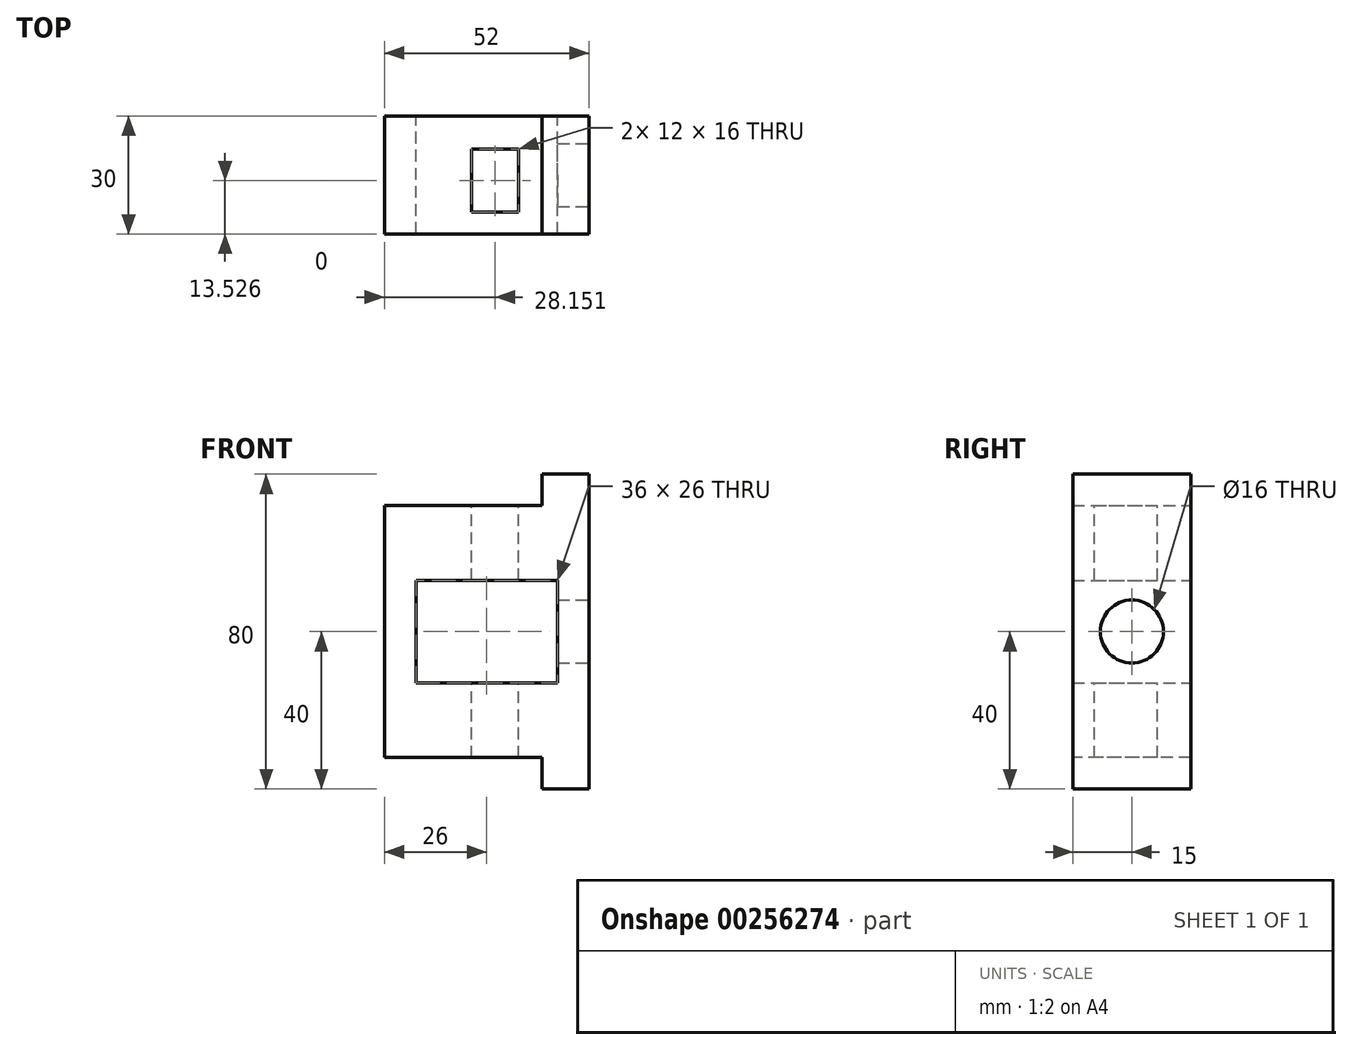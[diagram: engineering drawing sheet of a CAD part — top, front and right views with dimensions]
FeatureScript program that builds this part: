
annotation { "Feature Type Name" : "Feature", "Feature Type Description" : "" }
export const myFeature = defineFeature(function(context is Context, id is Id, definition is map)
    precondition{}
    {
        {
            var Q0;
            Q0=qCreatedBy(makeId("Right.planeOp"),FACE);
            var sketch = newSketch(context, id + "F0", { "sketchPlane" : qUnion([Q0])});
            skLineSegment(sketch, "E0.bottom", {"start": v(15, 32) * mm, "end": v(-15, 32) * mm});
            skLineSegment(sketch, "E0.top", {"start": v(15, -32) * mm, "end": v(-15, -32) * mm});
            skLineSegment(sketch, "E0.left", {"start": v(15, 32) * mm, "end": v(15, -32) * mm});
            skLineSegment(sketch, "E0.right", {"start": v(-15, 32) * mm, "end": v(-15, -32) * mm});
            skPoint(sketch, "E0.middle", {"position": v(0, 0) * mm});
            skSolve(sketch);
        }
        {
            var Q0;
            Q0=makeQuery(id+"F0.imprint","IMPRINT",FACE,{"disambiguationData":[TD([[makeQuery(id+"F0.imprint","IMPRINT",EDGE,{"derivedFrom":sQuery(id+"F0.wireOp",EDGE,"E0.bottom")}),1.0]])]});
            extrude(context, id + "F1", {"entities" : qUnion([Q0]), "depth" : 52 * mm});
        }
        {
            var Q0;
            Q0=makeQuery(id+"F1.opExtrude","SWEPT_FACE",FACE,{"disambiguationData":[OSD([sQuery(id+"F0.wireOp",EDGE,"E0.left")])]});
            var sketch = newSketch(context, id + "F2", { "sketchPlane" : qUnion([Q0])});
            skLineSegment(sketch, "E1.bottom", {"start": v(-8, -13) * mm, "end": v(-44, -13) * mm});
            skLineSegment(sketch, "E1.top", {"start": v(-8, 13) * mm, "end": v(-44, 13) * mm});
            skLineSegment(sketch, "E1.left", {"start": v(-8, -13) * mm, "end": v(-8, 13) * mm});
            skLineSegment(sketch, "E1.right", {"start": v(-44, -13) * mm, "end": v(-44, 13) * mm});
            skPoint(sketch, "E1.middle", {"position": v(-26, 0) * mm});
            skPoint(sketch, "E1.middle.positionSnap0", {"position": v(-26, 32) * mm});
            skPoint(sketch, "E1.middle.positionSnap1", {"position": v(-52, 0) * mm});
            skPoint(sketch, "E1.centerSnap0", {"position": v(-26, 32) * mm});
            skPoint(sketch, "E1.centerSnap1", {"position": v(-52, 0) * mm});
            skSolve(sketch);
        }
        {
            var Q0;
            Q0=makeQuery(id+"F2.imprint","IMPRINT",FACE,{"disambiguationData":[TD([[makeQuery(id+"F2.imprint","IMPRINT",EDGE,{"derivedFrom":sQuery(id+"F2.wireOp",EDGE,"E1.bottom")}),-1.0]])]});
            extrude(context, id + "F3", {"entities" : qUnion([Q0]), "operationType" : NewBodyOperationType.REMOVE, "oppositeDirection" : true, "depth" : 100 * mm});
        }
        {
            var Q0;
            Q0=makeQuery(id+"F1.opExtrude","SWEPT_FACE",FACE,{"disambiguationData":[OSD([sQuery(id+"F0.wireOp",EDGE,"E0.bottom")])]});
            var sketch = newSketch(context, id + "F4", { "sketchPlane" : qUnion([Q0])});
            skLineSegment(sketch, "E2.bottom", {"start": v(52, -15) * mm, "end": v(40, -15) * mm});
            skLineSegment(sketch, "E2.top", {"start": v(52, 15) * mm, "end": v(40, 15) * mm});
            skLineSegment(sketch, "E2.left", {"start": v(52, -15) * mm, "end": v(52, 15) * mm});
            skLineSegment(sketch, "E2.right", {"start": v(40, -15) * mm, "end": v(40, 15) * mm});
            skSolve(sketch);
        }
        {
            var Q0;
            Q0=makeQuery(id+"F4.imprint","IMPRINT",FACE,{"disambiguationData":[TD([[makeQuery(id+"F4.imprint","IMPRINT",EDGE,{"derivedFrom":sQuery(id+"F4.wireOp",EDGE,"E2.bottom")}),-1.0]])]});
            extrude(context, id + "F5", {"entities" : qUnion([Q0]), "operationType" : NewBodyOperationType.ADD, "depth" : 8 * mm});
        }
        {
            var Q0;
            Q0=makeQuery(id+"F1.opExtrude","SWEPT_FACE",FACE,{"disambiguationData":[OSD([sQuery(id+"F0.wireOp",EDGE,"E0.top")])]});
            var sketch = newSketch(context, id + "F6", { "sketchPlane" : qUnion([Q0])});
            skLineSegment(sketch, "E3.bottom", {"start": v(52, -15) * mm, "end": v(40, -15) * mm});
            skLineSegment(sketch, "E3.top", {"start": v(52, 15) * mm, "end": v(40, 15) * mm});
            skLineSegment(sketch, "E3.left", {"start": v(52, -15) * mm, "end": v(52, 15) * mm});
            skLineSegment(sketch, "E3.right", {"start": v(40, -15) * mm, "end": v(40, 15) * mm});
            skSolve(sketch);
        }
        {
            var Q0;
            Q0=makeQuery(id+"F6.imprint","IMPRINT",FACE,{"disambiguationData":[TD([[makeQuery(id+"F6.imprint","IMPRINT",EDGE,{"derivedFrom":sQuery(id+"F6.wireOp",EDGE,"E3.bottom")}),-1.0]])]});
            extrude(context, id + "F7", {"entities" : qUnion([Q0]), "operationType" : NewBodyOperationType.ADD, "depth" : 8 * mm});
        }
        {
            var Q0;
            Q0=makeQuery(id+"F7.boolean.opBoolean","MERGE",FACE,{"derivedFrom":[makeQuery(id+"F5.boolean.opBoolean","MERGE",FACE,{"derivedFrom":[makeQuery(id+"F1.opExtrude","CAP_FACE",FACE,{"disambiguationData":[OSD([sQuery(id+"F0.wireOp",EDGE,"E0.bottom"),sQuery(id+"F0.wireOp",EDGE,"E0.top"),sQuery(id+"F0.wireOp",EDGE,"E0.left"),sQuery(id+"F0.wireOp",EDGE,"E0.right")])],"isStart":false}),makeQuery(id+"F5.opExtrude","SWEPT_FACE",FACE,{"disambiguationData":[OSD([sQuery(id+"F4.wireOp",EDGE,"E2.left")])]})]}),makeQuery(id+"F7.opExtrude","SWEPT_FACE",FACE,{"disambiguationData":[OSD([sQuery(id+"F6.wireOp",EDGE,"E3.left")])]})]});
            var sketch = newSketch(context, id + "F8", { "sketchPlane" : qUnion([Q0])});
            skCircle(sketch, "E4", {"center": v(0, 0) * mm, "radius": 8 * mm});
            skSolve(sketch);
        }
        {
            var Q0;
            Q0=makeQuery(id+"F8.imprint","IMPRINT",FACE,{"disambiguationData":[TD([[makeQuery(id+"F8.imprint","IMPRINT",EDGE,{"derivedFrom":sQuery(id+"F8.wireOp",EDGE,"E4")}),1.0]])]});
            var Q1;
            Q1=sQuery(id+"F8.wireOp",EDGE,"E4");
            extrude(context, id + "F9", {"entities" : qUnion([Q0]), "operationType" : NewBodyOperationType.REMOVE, "surfaceEntities" : qUnion([Q1]), "oppositeDirection" : true, "depth" : 10 * mm});
        }
        {
            var Q0;
            Q0=makeQuery(id+"F1.opExtrude","SWEPT_FACE",FACE,{"disambiguationData":[OSD([sQuery(id+"F0.wireOp",EDGE,"E0.bottom")])]});
            var sketch = newSketch(context, id + "F10", { "sketchPlane" : qUnion([Q0])});
            skSolve(sketch);
        }
        {
            var Q0;
            {var subQ0=sQuery(id+"F0.wireOp",EDGE,"E0.bottom");Q0=makeQuery(id+"F10.imprint","IMPRINT",FACE,{"disambiguationData":[TD([[makeQuery(id+"F10.imprint","IMPRINT",EDGE,{"derivedFrom":makeQuery(id+"F1.opExtrude","CAP_EDGE",EDGE,{"disambiguationData":[OSD([subQ0])],"isStart":true})}),1.0]])]});}
            var sketch = newSketch(context, id + "F11", { "sketchPlane" : qUnion([Q0])});
            skLineSegment(sketch, "E5.bottom", {"start": v(22.15, -9.47) * mm, "end": v(34.15, -9.47) * mm});
            skLineSegment(sketch, "E5.top", {"start": v(22.15, 6.53) * mm, "end": v(34.15, 6.53) * mm});
            skLineSegment(sketch, "E5.left", {"start": v(22.15, -9.47) * mm, "end": v(22.15, 6.53) * mm});
            skLineSegment(sketch, "E5.right", {"start": v(34.15, -9.47) * mm, "end": v(34.15, 6.53) * mm});
            skSolve(sketch);
        }
        {
            var Q0;
            Q0=makeQuery(id+"F11.imprint","IMPRINT",FACE,{"disambiguationData":[TD([[makeQuery(id+"F11.imprint","IMPRINT",EDGE,{"derivedFrom":sQuery(id+"F11.wireOp",EDGE,"E5.bottom")}),1.0]])]});
            extrude(context, id + "F12", {"entities" : qUnion([Q0]), "operationType" : NewBodyOperationType.REMOVE, "oppositeDirection" : true, "depth" : 100 * mm});
        }
    });
